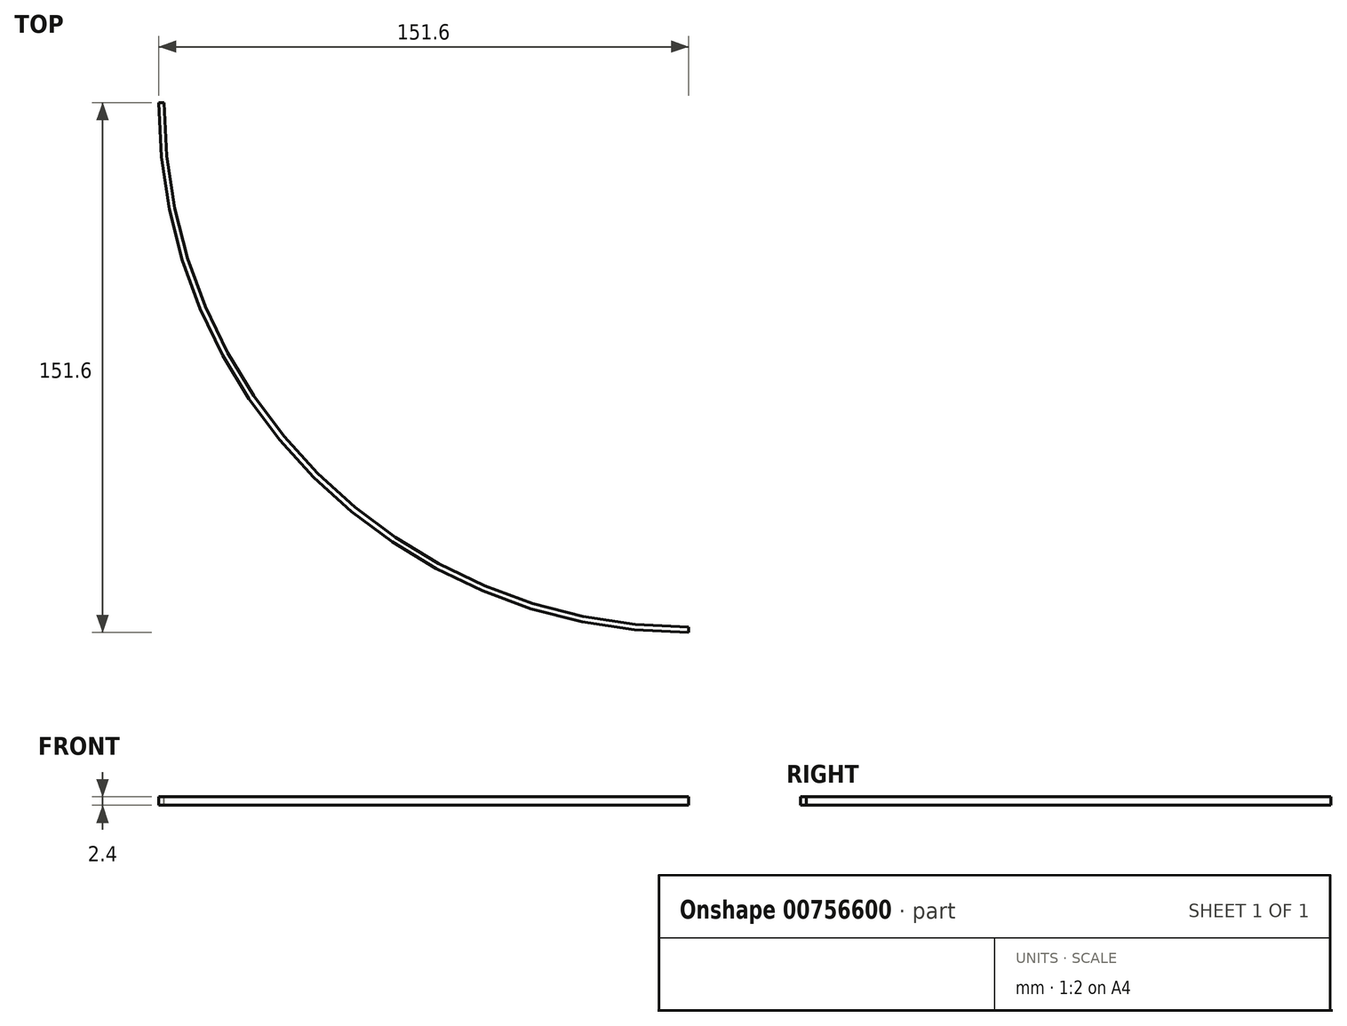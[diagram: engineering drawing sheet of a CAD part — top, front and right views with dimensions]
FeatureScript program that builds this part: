
annotation { "Feature Type Name" : "Feature", "Feature Type Description" : "" }
export const myFeature = defineFeature(function(context is Context, id is Id, definition is map)
    precondition{}
    {
        {
            var Q0;
            Q0=qCreatedBy(makeId("Front.planeOp"),FACE);
            var sketch = newSketch(context, id + "F0", { "sketchPlane" : qUnion([Q0])});
            skLineSegment(sketch, "E0.bottom", {"start": v(-37.75, 0) * mm, "end": v(-36.15, 0) * mm});
            skLineSegment(sketch, "E0.top", {"start": v(-37.75, 2.4) * mm, "end": v(-36.15, 2.4) * mm});
            skLineSegment(sketch, "E0.left", {"start": v(-37.75, 0) * mm, "end": v(-37.75, 2.4) * mm});
            skLineSegment(sketch, "E0.right", {"start": v(-36.15, 0) * mm, "end": v(-36.15, 2.4) * mm});
            skLineSegment(sketch, "E1", {"start": v(-36.15, 0) * mm, "end": v(113.85, 0) * mm});
            skLineSegment(sketch, "E2", {"start": v(113.85, 0) * mm, "end": v(113.85, 11.34) * mm});
            skSolve(sketch);
        }
        {
            var Q0;
            Q0=makeQuery(id+"F0.imprint","IMPRINT",FACE,{"disambiguationData":[TD([[makeQuery(id+"F0.imprint","IMPRINT",EDGE,{"derivedFrom":sQuery(id+"F0.wireOp",EDGE,"E0.bottom")}),1.0]])]});
            var Q1;
            Q1=sQuery(id+"F0.wireOp",EDGE,"E2");
            revolve(context, id + "F1", {"surfaceOperationType" : NewSurfaceOperationType.NEW, "entities" : qUnion([Q0]), "axis" : qUnion([Q1]), "revolveType" : RevolveType.ONE_DIRECTION, "angle" : 90 * degree});
        }
    });
